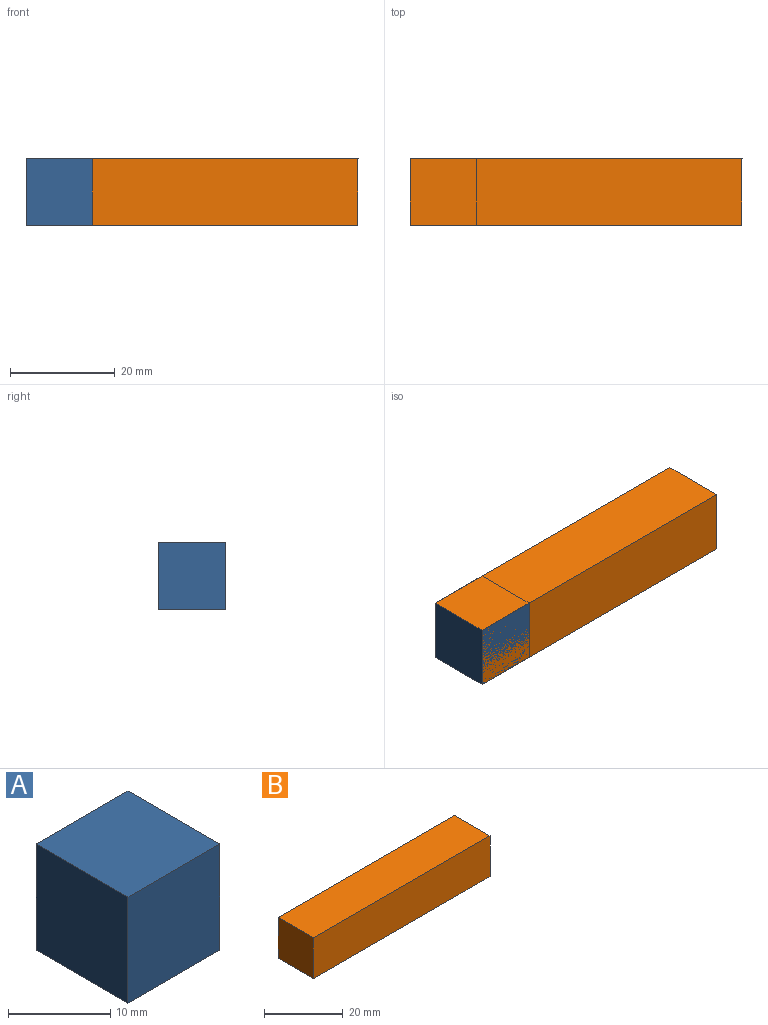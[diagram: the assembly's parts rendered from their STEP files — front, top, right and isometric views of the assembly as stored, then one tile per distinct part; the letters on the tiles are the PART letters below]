
ASSEMBLY  parts=2 mates=1
PART A: 6 faces, bbox 12.7x12.7x12.7 mm
  f0: plane 12.7x12.7mm, normal (0,0,-1), area 161.3mm2, adj f1,f3,f4,f5
  f1: plane 12.7x12.7mm, normal (1,0,0), area 161.3mm2, adj f0,f2,f4,f5
  f2: plane 12.7x12.7mm, normal (0,0,1), area 161.3mm2, adj f1,f3,f4,f5
  f3: plane 12.7x12.7mm, normal (-1,0,0), area 161.3mm2, adj f0,f2,f4,f5
  f4: plane 12.7x12.7mm, normal (0,-1,0), area 161.3mm2, adj f0,f1,f2,f3
  f5: plane 12.7x12.7mm, normal (0,1,0), area 161.3mm2, adj f0,f1,f2,f3
PART B: 6 faces, bbox 63.5x12.7x12.7 mm
  f0: plane 63.5x12.7mm, normal (0,0,-1), area 806.5mm2, adj f1,f3,f4,f5
  f1: plane 12.7x12.7mm, normal (1,0,0), area 161.3mm2, adj f0,f2,f4,f5
  f2: plane 63.5x12.7mm, normal (0,0,1), area 806.5mm2, adj f1,f3,f4,f5
  f3: plane 12.7x12.7mm, normal (-1,0,0), area 161.3mm2, adj f0,f2,f4,f5
  f4: plane 63.5x12.7mm, normal (0,-1,0), area 806.5mm2, adj f0,f1,f2,f3
  f5: plane 63.5x12.7mm, normal (0,1,0), area 806.5mm2, adj f0,f1,f2,f3
PLACE A rot(axis=(-0.25,0.16,-0.95),0deg) t=(-23.08,-17.62,-50.6)mm
PLACE B rot(axis=(-0.25,0.16,-0.95),0deg) t=(5.63,-17.62,21.58)mm
MATE slider B.f3 <-> A.f3  axis (-1,0,0) through (-29.43,-23.97,-22.03)mm
